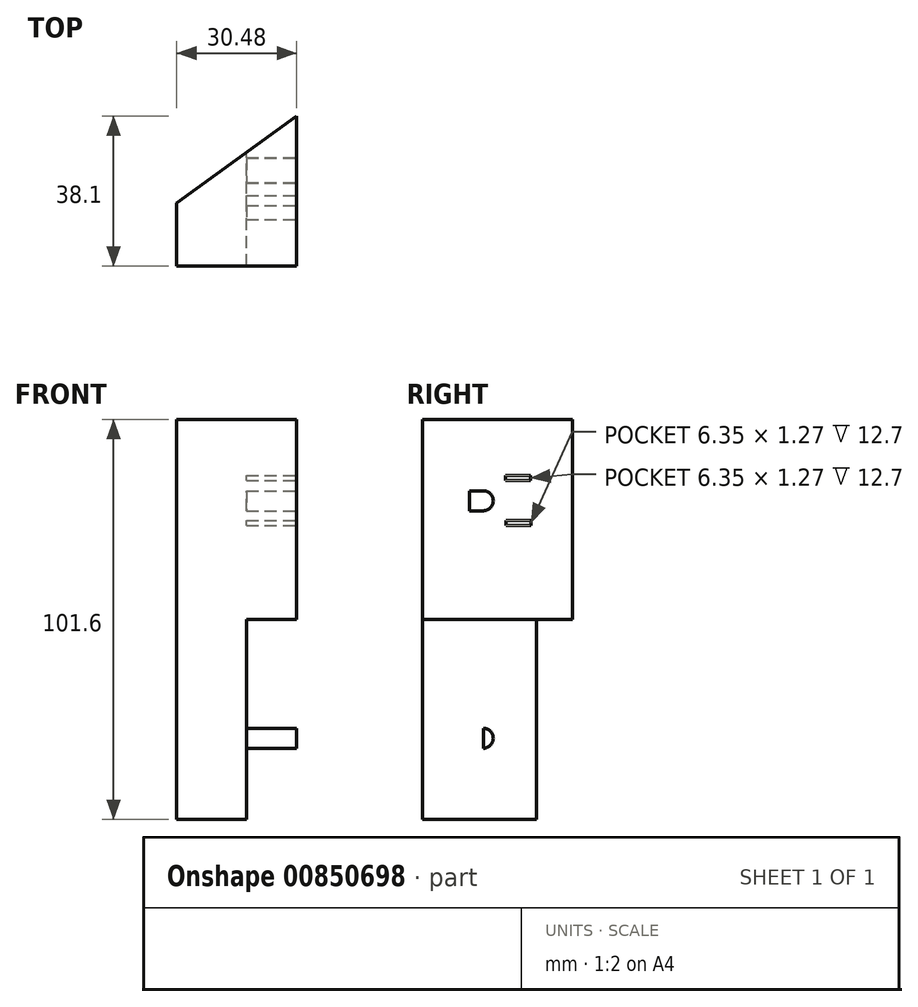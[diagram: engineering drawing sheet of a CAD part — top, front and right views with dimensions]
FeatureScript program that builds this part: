
annotation { "Feature Type Name" : "Feature", "Feature Type Description" : "" }
export const myFeature = defineFeature(function(context is Context, id is Id, definition is map)
    precondition{}
    {
        {
            var Q0;
            Q0=qCreatedBy(makeId("Top.planeOp"),FACE);
            var sketch = newSketch(context, id + "F0", { "sketchPlane" : qUnion([Q0])});
            skLineSegment(sketch, "E0", {"start": v(-30.48, 15.96) * mm, "end": v(-30.48, 0) * mm});
            skLineSegment(sketch, "E1", {"start": v(-30.48, 0) * mm, "end": v(0, 0) * mm});
            skLineSegment(sketch, "E2", {"start": v(0, 0) * mm, "end": v(0, 38.1) * mm});
            skLineSegment(sketch, "E3", {"start": v(0, 38.1) * mm, "end": v(-30.48, 15.96) * mm});
            skSolve(sketch);
        }
        {
            var Q0;
            Q0=makeQuery(id+"F0.imprint","IMPRINT",FACE,{"disambiguationData":[TD([[makeQuery(id+"F0.imprint","IMPRINT",EDGE,{"derivedFrom":sQuery(id+"F0.wireOp",EDGE,"E0")}),1.0]])]});
            extrude(context, id + "F1", {"entities" : qUnion([Q0]), "depth" : 101.6 * mm, "offsetDistance" : 25.4 * mm});
        }
        {
            var Q0;
            Q0=makeQuery(id+"F1.opExtrude","SWEPT_FACE",FACE,{"disambiguationData":[OSD([sQuery(id+"F0.wireOp",EDGE,"E2")])]});
            var sketch = newSketch(context, id + "F2", { "sketchPlane" : qUnion([Q0])});
            skLineSegment(sketch, "E4", {"start": v(27.44, 87.38) * mm, "end": v(21.1, 87.38) * mm});
            skLineSegment(sketch, "E5", {"start": v(21.1, 87.38) * mm, "end": v(21.1, 86.11) * mm});
            skLineSegment(sketch, "E6", {"start": v(21.1, 86.11) * mm, "end": v(27.44, 86.11) * mm});
            skLineSegment(sketch, "E7", {"start": v(27.44, 86.11) * mm, "end": v(27.44, 87.38) * mm});
            skLineSegment(sketch, "E8", {"start": v(27.52, 75.95) * mm, "end": v(21.17, 75.95) * mm});
            skLineSegment(sketch, "E9", {"start": v(21.17, 75.95) * mm, "end": v(21.17, 74.68) * mm});
            skLineSegment(sketch, "E10", {"start": v(21.17, 74.68) * mm, "end": v(27.52, 74.68) * mm});
            skLineSegment(sketch, "E11", {"start": v(27.52, 74.68) * mm, "end": v(27.52, 75.95) * mm});
            skLineSegment(sketch, "E12", {"start": v(24.27, 87.38) * mm, "end": v(24.27, 74.68) * mm, "construction": true});
            skLineSegment(sketch, "E13.bottom", {"start": v(15.41, 83.51) * mm, "end": v(11.87, 83.51) * mm});
            skLineSegment(sketch, "E13.top", {"start": v(15.41, 78.43) * mm, "end": v(11.87, 78.43) * mm});
            skLineSegment(sketch, "E13.left", {"start": v(15.41, 83.51) * mm, "end": v(15.41, 78.43) * mm});
            skLineSegment(sketch, "E13.right", {"start": v(11.87, 83.51) * mm, "end": v(11.87, 78.43) * mm});
            skArc(sketch, "E14", {"start": v(15.41, 78.43) * mm, "mid": v(17.95, 80.97) * mm, "end": v(15.41, 83.51) * mm});
            skLineSegment(sketch, "E15", {"start": v(38.1, 50.8) * mm, "end": v(0, 50.8) * mm});
            skLineSegment(sketch, "E16.MirrorCS", {"start": v(27.44, 14.22) * mm, "end": v(21.1, 14.22) * mm});
            skLineSegment(sketch, "E17.MirrorCS", {"start": v(27.44, 15.49) * mm, "end": v(27.44, 14.22) * mm});
            skLineSegment(sketch, "E18.MirrorCS", {"start": v(21.1, 15.49) * mm, "end": v(27.44, 15.49) * mm});
            skLineSegment(sketch, "E19.MirrorCS", {"start": v(21.1, 14.22) * mm, "end": v(21.1, 15.49) * mm});
            skLineSegment(sketch, "E20.MirrorCS", {"start": v(27.52, 25.65) * mm, "end": v(21.17, 25.65) * mm});
            skLineSegment(sketch, "E21.MirrorCS", {"start": v(27.52, 26.92) * mm, "end": v(27.52, 25.65) * mm});
            skLineSegment(sketch, "E22.MirrorCS", {"start": v(21.17, 26.92) * mm, "end": v(27.52, 26.92) * mm});
            skLineSegment(sketch, "E23.MirrorCS", {"start": v(21.17, 25.65) * mm, "end": v(21.17, 26.92) * mm});
            skArc(sketch, "E24.MirrorCS", {"start": v(15.41, 23.17) * mm, "mid": v(17.95, 20.63) * mm, "end": v(15.41, 18.09) * mm});
            skLineSegment(sketch, "E25.MirrorCS", {"start": v(15.41, 18.09) * mm, "end": v(11.87, 18.09) * mm});
            skLineSegment(sketch, "E26.MirrorCS", {"start": v(15.41, 18.09) * mm, "end": v(15.41, 23.17) * mm});
            skLineSegment(sketch, "E27.MirrorCS", {"start": v(15.41, 23.17) * mm, "end": v(11.87, 23.17) * mm});
            skLineSegment(sketch, "E28.MirrorCS", {"start": v(11.87, 18.09) * mm, "end": v(11.87, 23.17) * mm});
            skSolve(sketch);
        }
        {
            var Q0;
            Q0=makeQuery(id+"F2.imprint","IMPRINT",FACE,{"disambiguationData":[TD([[makeQuery(id+"F2.imprint","IMPRINT",EDGE,{"derivedFrom":sQuery(id+"F2.wireOp",EDGE,"E4")}),1.0]])]});
            var Q1;
            Q1=makeQuery(id+"F2.imprint","IMPRINT",FACE,{"disambiguationData":[TD([[makeQuery(id+"F2.imprint","IMPRINT",EDGE,{"derivedFrom":sQuery(id+"F2.wireOp",EDGE,"E8")}),1.0]])]});
            var Q2;
            Q2=makeQuery(id+"F2.imprint","IMPRINT",FACE,{"disambiguationData":[TD([[makeQuery(id+"F2.imprint","IMPRINT",EDGE,{"derivedFrom":sQuery(id+"F2.wireOp",EDGE,"E13.bottom")}),1.0]])]});
            var Q3;
            Q3=makeQuery(id+"F2.imprint","IMPRINT",FACE,{"disambiguationData":[TD([[makeQuery(id+"F2.imprint","IMPRINT",EDGE,{"derivedFrom":sQuery(id+"F2.wireOp",EDGE,"E13.left")}),1.0]])]});
            extrude(context, id + "F3", {"entities" : qUnion([Q0, Q1, Q2, Q3]), "operationType" : NewBodyOperationType.REMOVE, "oppositeDirection" : true, "depth" : 12.7 * mm, "offsetDistance" : 25.4 * mm});
        }
        {
            var Q0;
            Q0=makeQuery(id+"F2.imprint","IMPRINT",FACE,{"disambiguationData":[TD([[makeQuery(id+"F2.imprint","IMPRINT",EDGE,{"derivedFrom":sQuery(id+"F2.wireOp",EDGE,"E20.MirrorCS")}),-1.0]])]});
            var Q1;
            Q1=makeQuery(id+"F2.imprint","IMPRINT",FACE,{"disambiguationData":[TD([[makeQuery(id+"F2.imprint","IMPRINT",EDGE,{"derivedFrom":sQuery(id+"F2.wireOp",EDGE,"E16.MirrorCS")}),-1.0]])]});
            var Q2;
            Q2=makeQuery(id+"F2.imprint","IMPRINT",FACE,{"disambiguationData":[TD([[makeQuery(id+"F2.imprint","IMPRINT",EDGE,{"derivedFrom":sQuery(id+"F2.wireOp",EDGE,"E24.MirrorCS")}),-1.0]])]});
            var Q3;
            Q3=makeQuery(id+"F2.imprint","IMPRINT",FACE,{"disambiguationData":[TD([[makeQuery(id+"F2.imprint","IMPRINT",EDGE,{"derivedFrom":sQuery(id+"F2.wireOp",EDGE,"E25.MirrorCS")}),-1.0]])]});
            extrude(context, id + "F4", {"entities" : qUnion([Q0, Q1, Q2, Q3]), "operationType" : NewBodyOperationType.REMOVE, "oppositeDirection" : true, "depth" : 12.7 * mm, "offsetDistance" : 25.4 * mm});
        }
    });
